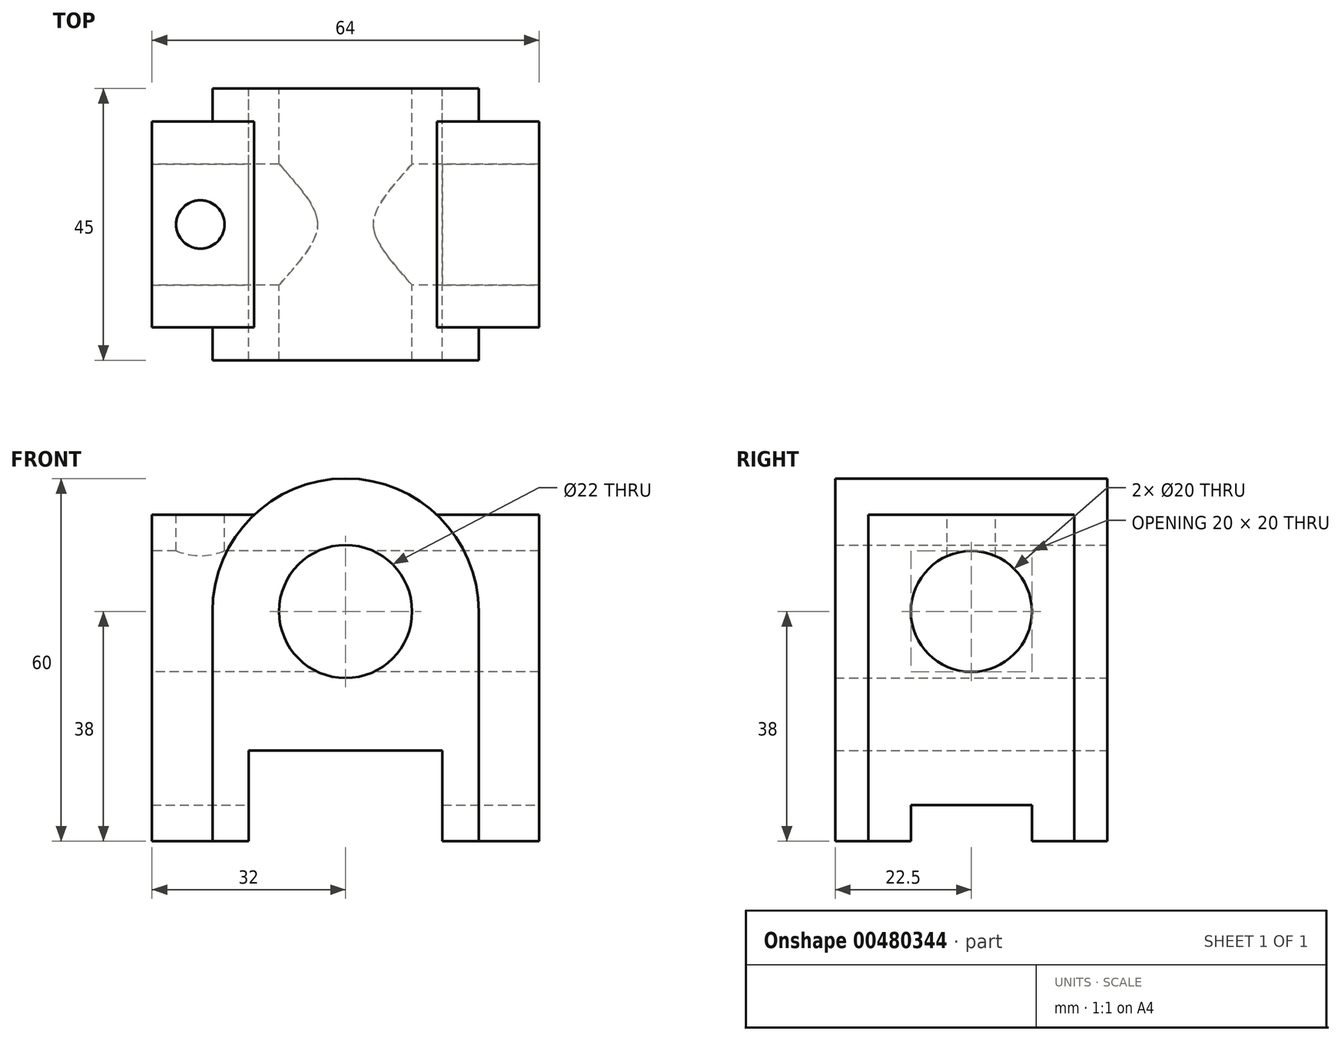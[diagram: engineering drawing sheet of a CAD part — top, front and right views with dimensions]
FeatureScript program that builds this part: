
annotation { "Feature Type Name" : "Feature", "Feature Type Description" : "" }
export const myFeature = defineFeature(function(context is Context, id is Id, definition is map)
    precondition{}
    {
        {
            var Q0;
            Q0=qCreatedBy(makeId("Front.planeOp"),FACE);
            var sketch = newSketch(context, id + "F0", { "sketchPlane" : qUnion([Q0])});
            skLineSegment(sketch, "E0", {"start": v(-22, 0) * mm, "end": v(-16, 0) * mm});
            skLineSegment(sketch, "E1", {"start": v(22, 0) * mm, "end": v(22, 38) * mm});
            skLineSegment(sketch, "E2", {"start": v(22, 38) * mm, "end": v(-22, 38) * mm, "construction": true});
            skLineSegment(sketch, "E3", {"start": v(-22, 38) * mm, "end": v(-22, 0) * mm});
            skArc(sketch, "E4", {"start": v(-22, 38) * mm, "mid": v(0, 60) * mm, "end": v(22, 38) * mm});
            skLineSegment(sketch, "E5", {"start": v(-16, 0) * mm, "end": v(-16, 15) * mm});
            skLineSegment(sketch, "E6", {"start": v(-16, 15) * mm, "end": v(16, 15) * mm});
            skLineSegment(sketch, "E7", {"start": v(16, 15) * mm, "end": v(16, 0) * mm});
            skLineSegment(sketch, "E8.trimOffspring", {"start": v(16, 0) * mm, "end": v(22, 0) * mm});
            skCircle(sketch, "E9", {"center": v(0, 38) * mm, "radius": 11 * mm});
            skLineSegment(sketch, "E10", {"start": v(-16, 0) * mm, "end": v(16, 0) * mm});
            skSolve(sketch);
        }
        {
            var Q0;
            Q0 = qSketchRegion(id + "F0", true);
            extrude(context, id + "F1", {"entities" : qUnion([Q0]), "endBound" : BoundingType.SYMMETRIC, "depth" : 45 * mm});
        }
        {
            var Q0;
            Q0=qCreatedBy(makeId("Right.planeOp"),FACE);
            var sketch = newSketch(context, id + "F2", { "sketchPlane" : qUnion([Q0])});
            skLineSegment(sketch, "E11.bottom", {"start": v(17, 54) * mm, "end": v(-17, 54) * mm});
            skLineSegment(sketch, "E11.top", {"start": v(17, 0) * mm, "end": v(10, 0) * mm});
            skLineSegment(sketch, "E11.left", {"start": v(17, 54) * mm, "end": v(17, 0) * mm});
            skLineSegment(sketch, "E11.right", {"start": v(-17, 54) * mm, "end": v(-17, 0) * mm});
            skLineSegment(sketch, "E12", {"start": v(10, 0) * mm, "end": v(10, 6) * mm});
            skLineSegment(sketch, "E13", {"start": v(10, 6) * mm, "end": v(-10, 6) * mm});
            skLineSegment(sketch, "E14", {"start": v(-10, 6) * mm, "end": v(-10, 0) * mm});
            skLineSegment(sketch, "E15.trimOffspring", {"start": v(-10, 0) * mm, "end": v(-17, 0) * mm});
            skLineSegment(sketch, "E16", {"start": v(0, 0) * mm, "end": v(0, 63.11) * mm, "construction": true});
            skPoint(sketch, "E16.endSnap0", {"position": v(0, 54) * mm});
            skCircle(sketch, "E17", {"center": v(0, 38) * mm, "radius": 10 * mm});
            skLineSegment(sketch, "E18", {"start": v(-10, 0) * mm, "end": v(10, 0) * mm});
            skSolve(sketch);
        }
        {
            var Q0;
            Q0 = qSketchRegion(id + "F2", true);
            extrude(context, id + "F3", {"entities" : qUnion([Q0]), "operationType" : NewBodyOperationType.ADD, "endBound" : BoundingType.SYMMETRIC, "depth" : 64 * mm});
        }
        {
            var Q0;
            Q0=makeQuery(id+"F1.opExtrude","CAP_FACE",FACE,{"disambiguationData":[OSD([sQuery(id+"F0.wireOp",EDGE,"E0"),sQuery(id+"F0.wireOp",EDGE,"E1"),sQuery(id+"F0.wireOp",EDGE,"E3"),sQuery(id+"F0.wireOp",EDGE,"E4"),sQuery(id+"F0.wireOp",EDGE,"E5"),sQuery(id+"F0.wireOp",EDGE,"E6"),sQuery(id+"F0.wireOp",EDGE,"E7"),sQuery(id+"F0.wireOp",EDGE,"E8.trimOffspring"),sQuery(id+"F0.wireOp",EDGE,"E9")])],"isStart":false});
            var sketch = newSketch(context, id + "F4", { "sketchPlane" : qUnion([Q0])});
            skCircle(sketch, "E19.0", {"center": v(0, 38) * mm, "radius": 11 * mm});
            skSolve(sketch);
        }
        {
            var Q0;
            Q0 = qSketchRegion(id + "F4", true);
            extrude(context, id + "F5", {"entities" : qUnion([Q0]), "operationType" : NewBodyOperationType.REMOVE, "endBound" : BoundingType.THROUGH_ALL, "oppositeDirection" : true, "depth" : 25 * mm});
        }
        {
            var Q0;
            Q0=makeQuery(id+"F3.opExtrude","CAP_FACE",FACE,{"disambiguationData":[OSD([sQuery(id+"F2.wireOp",EDGE,"E11.bottom"),sQuery(id+"F2.wireOp",EDGE,"E11.top"),sQuery(id+"F2.wireOp",EDGE,"E11.left"),sQuery(id+"F2.wireOp",EDGE,"E11.right"),sQuery(id+"F2.wireOp",EDGE,"E12"),sQuery(id+"F2.wireOp",EDGE,"E13"),sQuery(id+"F2.wireOp",EDGE,"E14"),sQuery(id+"F2.wireOp",EDGE,"E15.trimOffspring"),sQuery(id+"F2.wireOp",EDGE,"E17")])],"isStart":true});
            var sketch = newSketch(context, id + "F6", { "sketchPlane" : qUnion([Q0])});
            skCircle(sketch, "E20.0", {"center": v(0, 38) * mm, "radius": 10 * mm});
            skSolve(sketch);
        }
        {
            var Q0;
            Q0 = qSketchRegion(id + "F6", true);
            extrude(context, id + "F7", {"entities" : qUnion([Q0]), "operationType" : NewBodyOperationType.REMOVE, "endBound" : BoundingType.THROUGH_ALL, "oppositeDirection" : true, "depth" : 25 * mm});
        }
        {
            var Q0;
            Q0=makeQuery(id+"F3.opExtrude","CAP_FACE",FACE,{"disambiguationData":[OSD([sQuery(id+"F2.wireOp",EDGE,"E11.bottom"),sQuery(id+"F2.wireOp",EDGE,"E11.top"),sQuery(id+"F2.wireOp",EDGE,"E11.left"),sQuery(id+"F2.wireOp",EDGE,"E11.right"),sQuery(id+"F2.wireOp",EDGE,"E15.trimOffspring"),sQuery(id+"F2.wireOp",EDGE,"E17"),sQuery(id+"F2.wireOp",EDGE,"E18")])],"isStart":false});
            var sketch = newSketch(context, id + "F8", { "sketchPlane" : qUnion([Q0])});
            skLineSegment(sketch, "E21.0", {"start": v(10, 0) * mm, "end": v(10, 6) * mm});
            skLineSegment(sketch, "E22.0", {"start": v(-10, 6) * mm, "end": v(-10, 0) * mm});
            skLineSegment(sketch, "E23", {"start": v(-10, 6) * mm, "end": v(10, 6) * mm});
            skLineSegment(sketch, "E24.0", {"start": v(-10, 0) * mm, "end": v(10, 0) * mm});
            skPoint(sketch, "E25.orphan", {"position": v(-17, 0) * mm});
            skPoint(sketch, "E26.orphan", {"position": v(17, 0) * mm});
            skSolve(sketch);
        }
        {
            var Q0;
            Q0 = qSketchRegion(id + "F8", true);
            extrude(context, id + "F9", {"entities" : qUnion([Q0]), "operationType" : NewBodyOperationType.REMOVE, "endBound" : BoundingType.THROUGH_ALL, "oppositeDirection" : true, "depth" : 25 * mm});
        }
        {
            var Q0;
            Q0=makeQuery(id+"F1.opExtrude","CAP_FACE",FACE,{"disambiguationData":[OSD([sQuery(id+"F0.wireOp",EDGE,"E0"),sQuery(id+"F0.wireOp",EDGE,"E1"),sQuery(id+"F0.wireOp",EDGE,"E3"),sQuery(id+"F0.wireOp",EDGE,"E4"),sQuery(id+"F0.wireOp",EDGE,"E8.trimOffspring"),sQuery(id+"F0.wireOp",EDGE,"E9"),sQuery(id+"F0.wireOp",EDGE,"E10")])],"isStart":true});
            var sketch = newSketch(context, id + "F10", { "sketchPlane" : qUnion([Q0])});
            skLineSegment(sketch, "E27.0", {"start": v(-16, 15) * mm, "end": v(-16, 0) * mm});
            skLineSegment(sketch, "E28.0", {"start": v(16, 15) * mm, "end": v(-16, 15) * mm});
            skLineSegment(sketch, "E29.0", {"start": v(16, 0) * mm, "end": v(16, 15) * mm});
            skLineSegment(sketch, "E30.0", {"start": v(16, 0) * mm, "end": v(-16, 0) * mm});
            skPoint(sketch, "E31.orphan", {"position": v(-22, 0) * mm});
            skPoint(sketch, "E32.orphan", {"position": v(22, 0) * mm});
            skSolve(sketch);
        }
        {
            var Q0;
            Q0 = qSketchRegion(id + "F10", true);
            extrude(context, id + "F11", {"entities" : qUnion([Q0]), "operationType" : NewBodyOperationType.REMOVE, "endBound" : BoundingType.THROUGH_ALL, "oppositeDirection" : true, "depth" : 25 * mm});
        }
        {
            var Q0;
            {var subQ0=sQuery(id+"F2.wireOp",EDGE,"E11.right");var subQ1=sQuery(id+"F2.wireOp",EDGE,"E11.left");var subQ2=sQuery(id+"F2.wireOp",EDGE,"E11.bottom");Q0=makeQuery(id+"F3.boolean.opBoolean","SPLIT",FACE,{"disambiguationData":[TD([makeQuery(id+"F3.opExtrude","CAP_FACE",FACE,{"disambiguationData":[OSD([subQ2,sQuery(id+"F2.wireOp",EDGE,"E11.top"),subQ1,subQ0,sQuery(id+"F2.wireOp",EDGE,"E12"),sQuery(id+"F2.wireOp",EDGE,"E13"),sQuery(id+"F2.wireOp",EDGE,"E14"),sQuery(id+"F2.wireOp",EDGE,"E15.trimOffspring"),sQuery(id+"F2.wireOp",EDGE,"E17")])],"isStart":true})])],"derivedFrom":makeQuery(id+"F3.opExtrude","SWEPT_FACE",FACE,{"disambiguationData":[OSD([subQ2])]})});}
            var sketch = newSketch(context, id + "F12", { "sketchPlane" : qUnion([Q0])});
            skLineSegment(sketch, "E33", {"start": v(-32, 0) * mm, "end": v(32.19, 0) * mm, "construction": true});
            skCircle(sketch, "E34", {"center": v(-24, 0) * mm, "radius": 4 * mm});
            skSolve(sketch);
        }
        {
            var Q0;
            Q0 = qSketchRegion(id + "F12", true);
            extrude(context, id + "F13", {"entities" : qUnion([Q0]), "operationType" : NewBodyOperationType.REMOVE, "oppositeDirection" : true, "depth" : 15 * mm});
        }
    });
